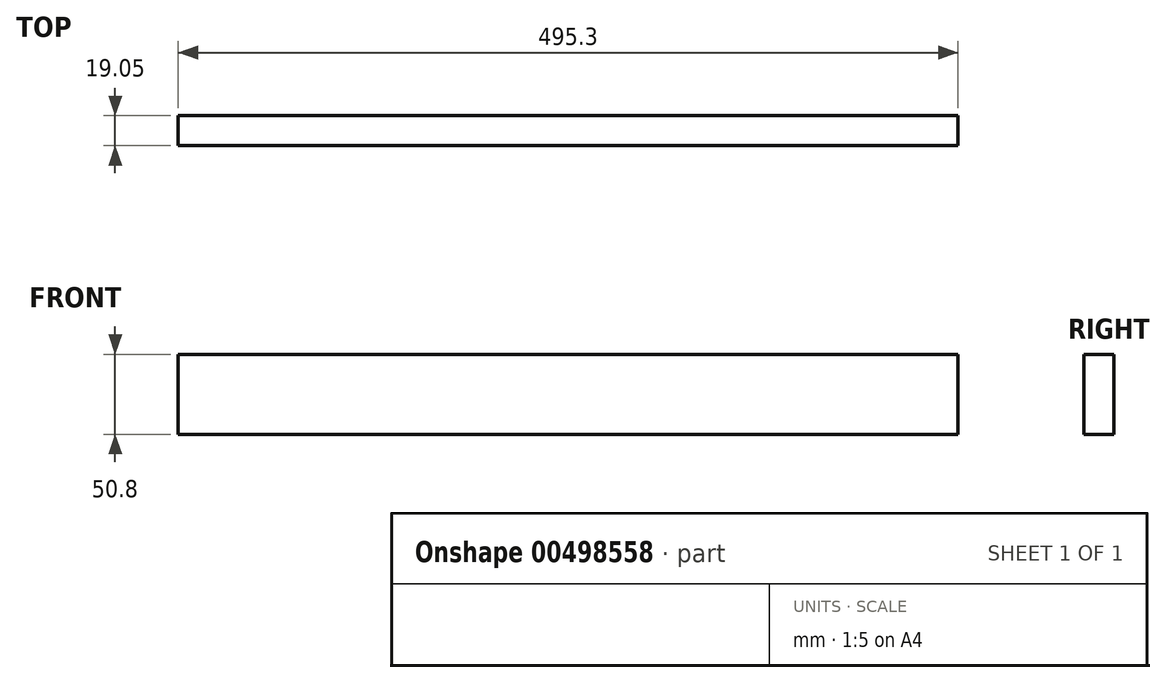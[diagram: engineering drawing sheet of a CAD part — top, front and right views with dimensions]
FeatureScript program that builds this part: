
annotation { "Feature Type Name" : "Feature", "Feature Type Description" : "" }
export const myFeature = defineFeature(function(context is Context, id is Id, definition is map)
    precondition{}
    {
        {
            var Q0;
            Q0=qCreatedBy(makeId("Front.planeOp"),FACE);
            var sketch = newSketch(context, id + "F0", { "sketchPlane" : qUnion([Q0])});
            skLineSegment(sketch, "E0.bottom", {"start": v(0, 0) * mm, "end": v(495.3, 0) * mm});
            skLineSegment(sketch, "E0.top", {"start": v(0, 50.8) * mm, "end": v(495.3, 50.8) * mm});
            skLineSegment(sketch, "E0.left", {"start": v(0, 0) * mm, "end": v(0, 50.8) * mm});
            skLineSegment(sketch, "E0.right", {"start": v(495.3, 0) * mm, "end": v(495.3, 50.8) * mm});
            skSolve(sketch);
        }
        {
            var Q0;
            Q0 = qSketchRegion(id + "F0", true);
            extrude(context, id + "F1", {"entities" : qUnion([Q0]), "depth" : 19.05 * mm, "offsetDistance" : 25.4 * mm});
        }
    });
